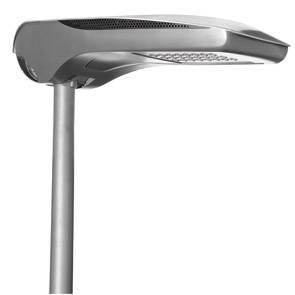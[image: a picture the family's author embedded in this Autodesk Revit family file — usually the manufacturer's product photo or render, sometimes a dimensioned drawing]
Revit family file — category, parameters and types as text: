
# Revit family: Lighting-Stradale-GEWISS-STREET[O3]-ARMATURE-LED_OTTICA_ST1
name_source: partatom
category: Apparecchi per illuminazione
units: mm (PartAtom-declared; Revit-internal decimal feet)

## family parameters
Basato su piano di lavoro = No
Condiviso = No
Numero OmniClass = 23.80.70.14.21
Punto di calcolo locali = No
Quota connettore circolare = Usa diametro
Sempre verticale = Sì
Sorgente d'illuminazione = No
Taglio con vuoti quando caricato = No
Tipo di parte = Normale
Titolo OmniClass = Street and Roadway Lighting

## types (1)
- Lighting-Stradale-GEWISS-STREET[O3]-ARMATURE-LED_OTTICA_ST1
    Altezza da terra testa staffa = 822 mm
    Applicazione = Esterno
    Carico apparente = 68 VA
    Catalogo = LIGHTING
    Catalogo Serie = STREET [O3]
    Classe isolamento = II
    Codice Electrocod = 244C
    Colore = Grafite/Alluminio
    Commenti sul wattaggio = 68W
    Corrente di pilotaggio LED = 700 mA
    Descrizione = STREET LED 2M 4000K 700mA STR
    Distanza minima dall'oggetto illuminato = 1M
    Flusso nominale (lm) = 8050
    Garanzia = 5 anni
    Grado di protezione = IP66
    IDF = e0084f90-0bca-44b3-a72f-039b3bfef071
    IDT = a85e433dc89b4111a164f9b8ba35bb1e
    Immagine tipo = GW87502.jpg
    LED Life time (L80B10) = 100000H
    LED LifeTime (L90B20) = 50000H
    L_staffa = 120 mm  [stored 0.393701 ft]
    Lampada = LED
    Lampada: = LED
    Lumen output (lm) = 6760
    Modello = GW87411V
    Numero di poli = 2
    Numero moduli = 2 (2x16 LED)
    Ottica = ST1 - ULOR: 0%
    Peso (kg): = 9,09999999999999
    Potenza di sistema = 68W
    Produttore = GEWISS S.p.A.
    Regolazione inclinazione = ±20° sbraccio - 0°÷20° testa palo
    Resistenza agli urti = IK08 CORPO - IK06 LENTI
    Rischio fotobiologico: = RG1/RG2 @ 20cm
    SEO = Stradale
    Scheda Tecnica = https://www.gewiss.com
    Struttura = <Per categoria>
    Superficie massima esposta al vento = 0,26M2
    Temperatura di colore: = 4000 K (CRI>70)
    Temperatura di utilizzo = -25 +25 °C
    Tensione = 220/240 V - 50/60 Hz - Stand alone e/o Programmabile 5 Step
    Tensione: = 220/240 V - 50/60 Hz
    Tipologia = Programmabile (5 passi)
    URL = https://www.gewiss.com
    Versione file RFA = 20.11
    Vetro = GEWISS - Led - lm 650 / Temp_3000_K
    Voltaggio = 230 V

note: [stored X ft] marks values corroborated as IEEE doubles in the binary element streams (Revit-internal decimal feet)
